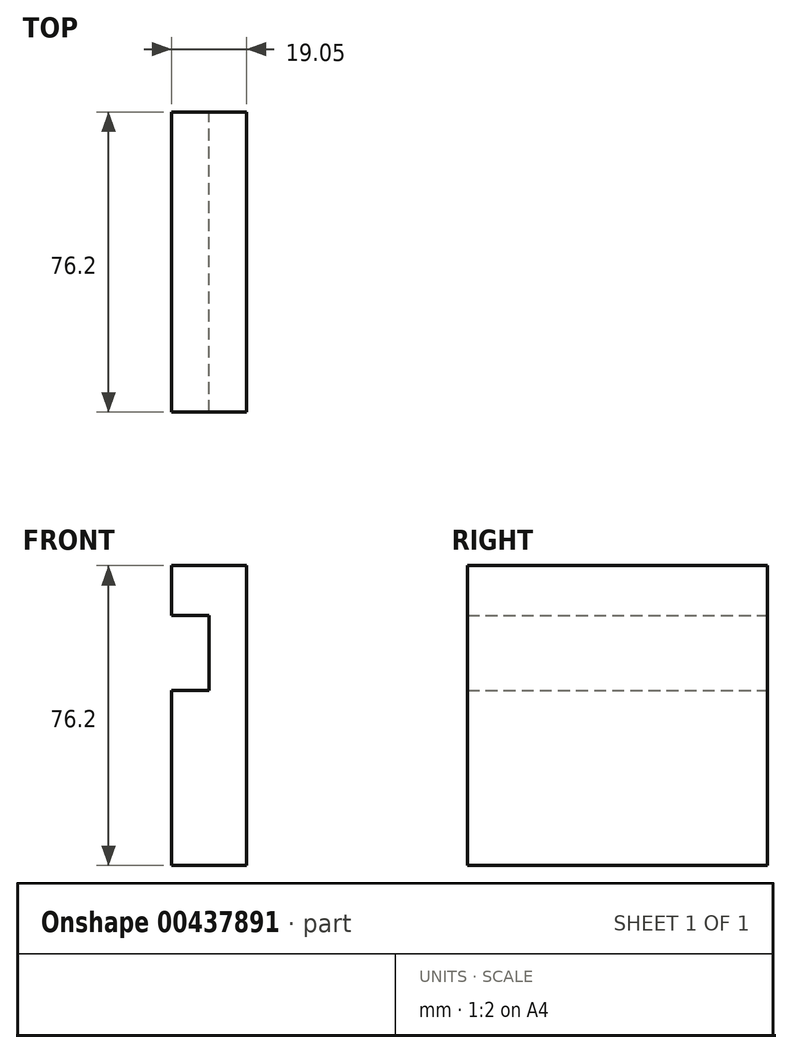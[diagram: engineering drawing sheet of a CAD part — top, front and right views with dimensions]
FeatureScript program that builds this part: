
annotation { "Feature Type Name" : "Feature", "Feature Type Description" : "" }
export const myFeature = defineFeature(function(context is Context, id is Id, definition is map)
    precondition{}
    {
        {
            var Q0;
            Q0=qCreatedBy(makeId("Front.planeOp"),FACE);
            var sketch = newSketch(context, id + "F0", { "sketchPlane" : qUnion([Q0])});
            skLineSegment(sketch, "E0", {"start": v(11.98, -20.86) * mm, "end": v(11.98, 55.34) * mm});
            skLineSegment(sketch, "E1", {"start": v(11.98, 55.34) * mm, "end": v(-7.07, 55.34) * mm});
            skLineSegment(sketch, "E2", {"start": v(-7.07, 55.34) * mm, "end": v(-7.07, 42.72) * mm});
            skLineSegment(sketch, "E3", {"start": v(11.98, -20.86) * mm, "end": v(-7.07, -20.86) * mm});
            skLineSegment(sketch, "E4", {"start": v(-7.07, 23.67) * mm, "end": v(-7.07, -20.86) * mm});
            skLineSegment(sketch, "E5", {"start": v(-7.07, 42.72) * mm, "end": v(2.46, 42.72) * mm});
            skLineSegment(sketch, "E6", {"start": v(-7.07, 23.67) * mm, "end": v(2.46, 23.67) * mm});
            skLineSegment(sketch, "E7", {"start": v(2.46, 23.67) * mm, "end": v(2.46, 42.72) * mm});
            skSolve(sketch);
        }
        {
            var Q0;
            Q0 = qSketchRegion(id + "F0", true);
            extrude(context, id + "F1", {"entities" : qUnion([Q0]), "depth" : 76.2 * mm});
        }
    });
